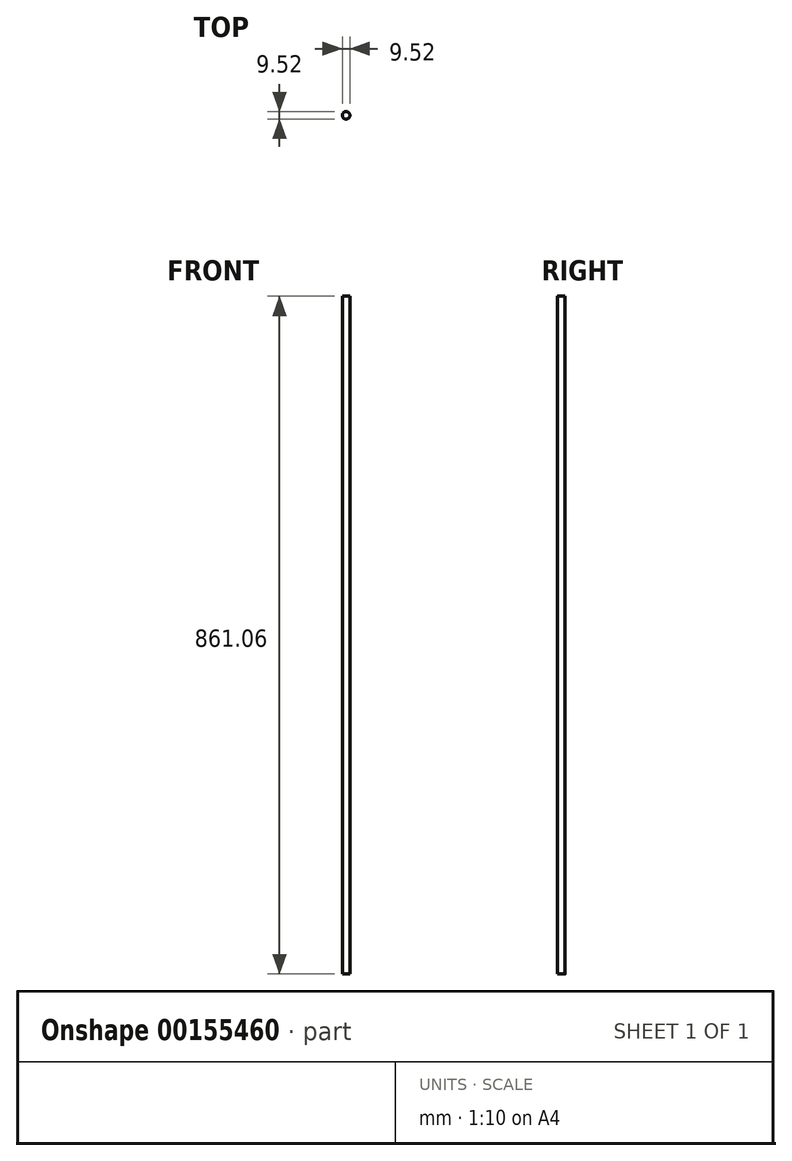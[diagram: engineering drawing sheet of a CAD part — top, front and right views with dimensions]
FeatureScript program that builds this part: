
annotation { "Feature Type Name" : "Feature", "Feature Type Description" : "" }
export const myFeature = defineFeature(function(context is Context, id is Id, definition is map)
    precondition{}
    {
        {
            var Q0;
            Q0=qCreatedBy(makeId("Top.planeOp"),FACE);
            var sketch = newSketch(context, id + "F0", { "sketchPlane" : qUnion([Q0])});
            skCircle(sketch, "E0", {"center": v(0, 0) * mm, "radius": 4.76 * mm});
            skSolve(sketch);
        }
        {
            var Q0;
            Q0 = qSketchRegion(id + "F0", true);
            extrude(context, id + "F1", {"entities" : qUnion([Q0]), "depth" : 861.06 * mm});
        }
    });
